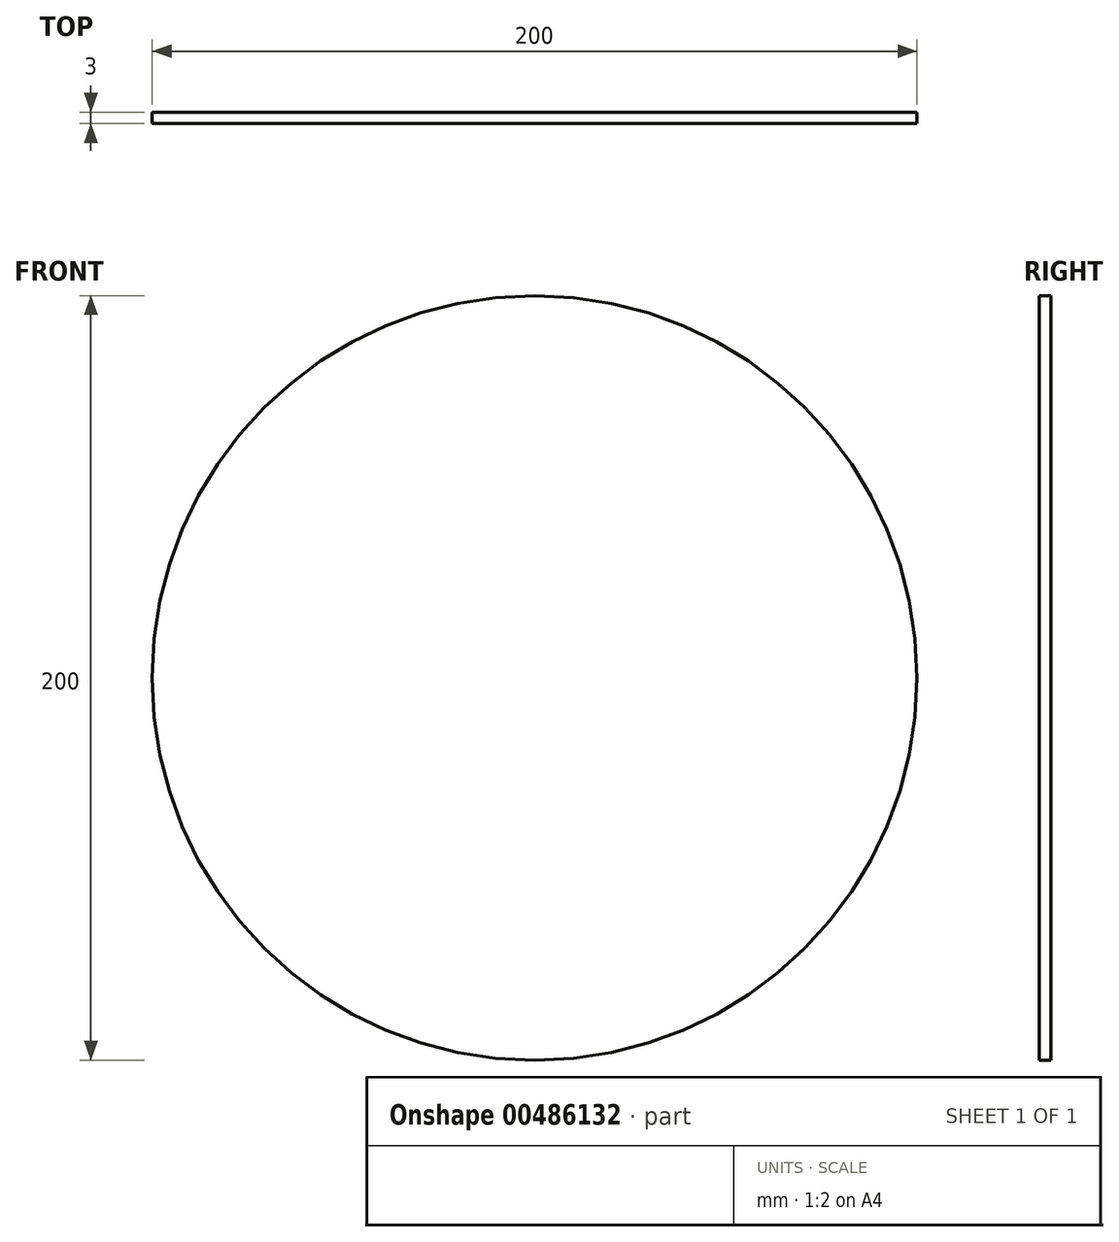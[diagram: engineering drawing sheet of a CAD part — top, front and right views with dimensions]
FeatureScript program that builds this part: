
annotation { "Feature Type Name" : "Feature", "Feature Type Description" : "" }
export const myFeature = defineFeature(function(context is Context, id is Id, definition is map)
    precondition{}
    {
        {
            var Q0;
            Q0=qCreatedBy(makeId("Front.planeOp"),FACE);
            var sketch = newSketch(context, id + "F0", { "sketchPlane" : qUnion([Q0])});
            skCircle(sketch, "E0", {"center": v(0, 0) * mm, "radius": 100 * mm});
            skSolve(sketch);
        }
        {
            var Q0;
            Q0 = qSketchRegion(id + "F0", true);
            extrude(context, id + "F1", {"entities" : qUnion([Q0]), "depth" : 3 * mm});
        }
    });
